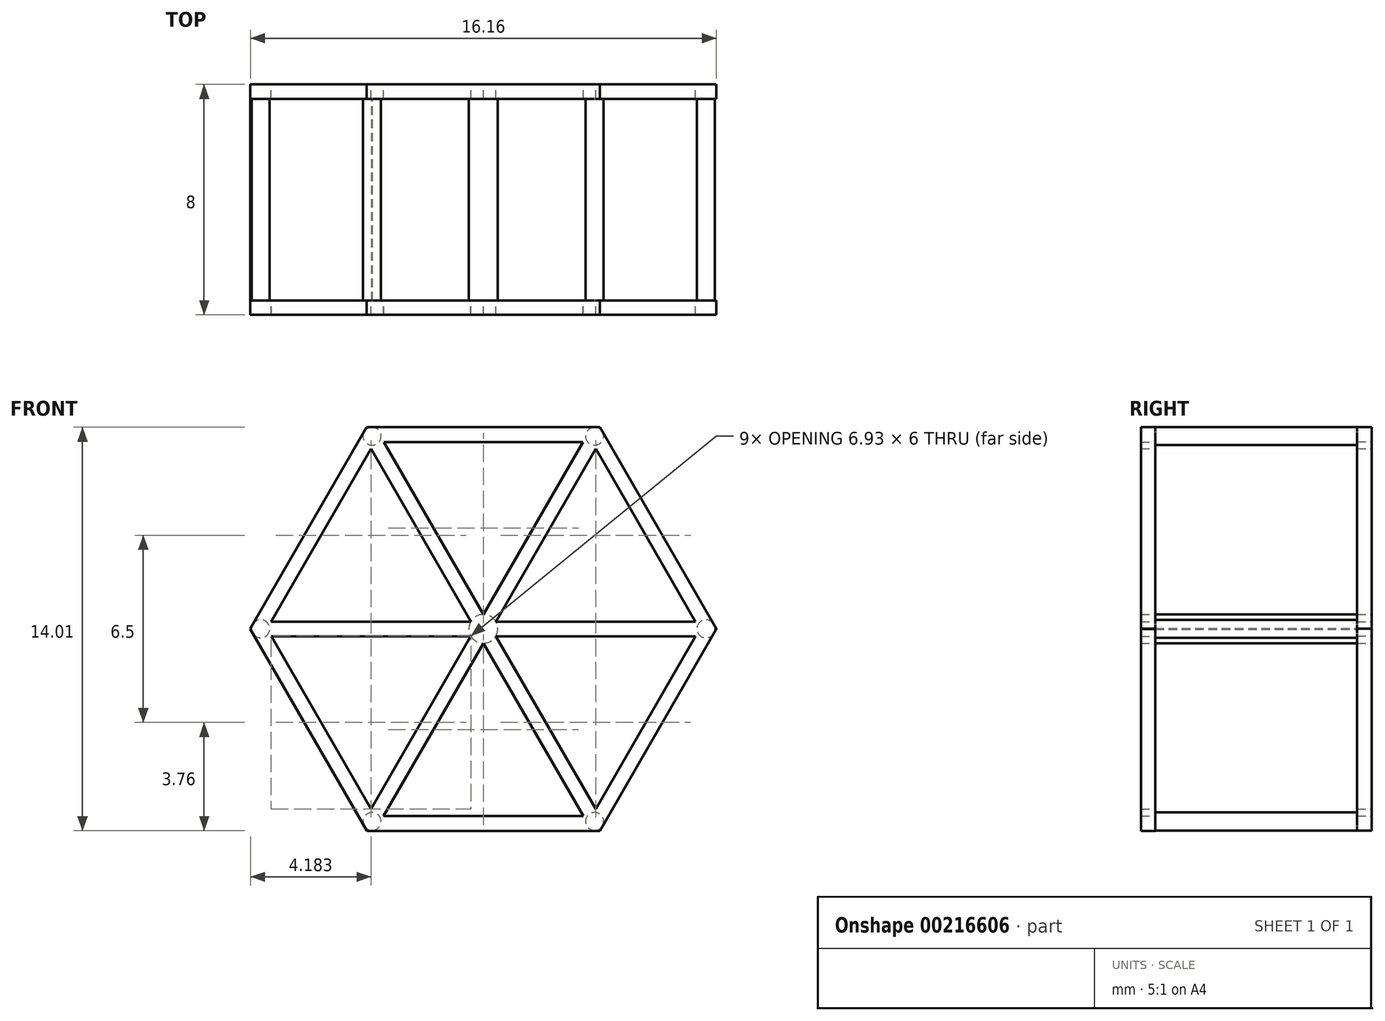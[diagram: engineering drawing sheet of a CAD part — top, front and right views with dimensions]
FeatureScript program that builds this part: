
annotation { "Feature Type Name" : "Feature", "Feature Type Description" : "" }
export const myFeature = defineFeature(function(context is Context, id is Id, definition is map)
    precondition{}
    {
        {
            var Q0;
            Q0=qCreatedBy(makeId("Front.planeOp"),FACE);
            var sketch = newSketch(context, id + "F0", { "sketchPlane" : qUnion([Q0])});
            skLineSegment(sketch, "E0.0", {"start": v(-4.04, 7) * mm, "end": v(4.04, 7) * mm});
            skLineSegment(sketch, "E0.1", {"start": v(4.04, 7) * mm, "end": v(8.08, 0) * mm});
            skLineSegment(sketch, "E0.2", {"start": v(8.08, 0) * mm, "end": v(4.04, -7) * mm});
            skLineSegment(sketch, "E0.3", {"start": v(4.04, -7) * mm, "end": v(-4.04, -7) * mm});
            skLineSegment(sketch, "E0.4", {"start": v(-4.04, -7) * mm, "end": v(-8.08, 0) * mm});
            skLineSegment(sketch, "E0.5", {"start": v(-8.08, 0) * mm, "end": v(-4.04, 7) * mm});
            skPoint(sketch, "E0.0.midPoint", {"position": v(0, 7) * mm});
            skLineSegment(sketch, "E1.0", {"start": v(-3.46, 6.5) * mm, "end": v(3.75, 6.5) * mm});
            skLineSegment(sketch, "E1.1", {"start": v(3.75, 6.5) * mm, "end": v(7.5, 0) * mm});
            skLineSegment(sketch, "E1.2", {"start": v(7.5, 0) * mm, "end": v(3.75, -6.5) * mm});
            skLineSegment(sketch, "E1.3", {"start": v(3.75, -6.5) * mm, "end": v(-3.46, -6.5) * mm});
            skLineSegment(sketch, "E1.4", {"start": v(-3.75, -6.5) * mm, "end": v(-7.36, -0.25) * mm});
            skLineSegment(sketch, "E1.5", {"start": v(-7.36, 0.25) * mm, "end": v(-3.9, 6.25) * mm});
            skPoint(sketch, "E1.0.midPoint", {"position": v(0, 6.5) * mm});
            skLineSegment(sketch, "E2", {"start": v(-0.43, 0.25) * mm, "end": v(-7.36, 0.25) * mm});
            skLineSegment(sketch, "E3", {"start": v(-0.43, -0.25) * mm, "end": v(-7.36, -0.25) * mm});
            skLineSegment(sketch, "E4.1.1", {"start": v(-0.43, -0.25) * mm, "end": v(-3.9, -6.25) * mm});
            skLineSegment(sketch, "E4.2.1", {"start": v(0, -0.5) * mm, "end": v(3.46, -6.5) * mm});
            skLineSegment(sketch, "E4.2.3", {"start": v(0.43, -0.25) * mm, "end": v(3.9, -6.25) * mm});
            skLineSegment(sketch, "E4.2.5", {"start": v(3.75, -6.5) * mm, "end": v(0, -6.5) * mm});
            skLineSegment(sketch, "E4.3.1", {"start": v(0, -0.25) * mm, "end": v(0.14, -0.25) * mm});
            skLineSegment(sketch, "E4.3.3", {"start": v(0.43, 0.25) * mm, "end": v(7.36, 0.25) * mm});
            skLineSegment(sketch, "E4.4.1", {"start": v(0.43, 0.25) * mm, "end": v(3.9, 6.25) * mm});
            skLineSegment(sketch, "E4.4.3", {"start": v(0, 0.5) * mm, "end": v(3.46, 6.5) * mm});
            skLineSegment(sketch, "E4.4.6", {"start": v(-3.75, 6.5) * mm, "end": v(3.75, 6.5) * mm});
            skLineSegment(sketch, "E4.5.1", {"start": v(0, 0.5) * mm, "end": v(-3.46, 6.5) * mm});
            skLineSegment(sketch, "E4.5.5", {"start": v(-3.75, 6.5) * mm, "end": v(3.75, 6.5) * mm});
            skPoint(sketch, "E4.center", {"position": v(0, 0) * mm});
            skPoint(sketch, "E5.orphan", {"position": v(-7.5, 0) * mm});
            skPoint(sketch, "E6.orphan", {"position": v(-0.22, 0.13) * mm});
            skPoint(sketch, "E7.orphan", {"position": v(0.22, 0.13) * mm});
            skPoint(sketch, "E8.orphan", {"position": v(0.22, -0.13) * mm});
            skLineSegment(sketch, "E9.trimOffspring", {"start": v(-0.43, 0.25) * mm, "end": v(-3.9, 6.25) * mm});
            skLineSegment(sketch, "E10.trimOffspring", {"start": v(0, -0.5) * mm, "end": v(-3.46, -6.5) * mm});
            skLineSegment(sketch, "E11.trimOffspring", {"start": v(0.43, -0.25) * mm, "end": v(7.36, -0.25) * mm});
            skPoint(sketch, "E12.orphan", {"position": v(0, -0.25) * mm});
            skLineSegment(sketch, "E13", {"start": v(0, 6.5) * mm, "end": v(0, 0.5) * mm});
            skPoint(sketch, "E14.orphan", {"position": v(-3.75, 6.5) * mm});
            skPoint(sketch, "E15.trimOffspring.end.orphan", {"position": v(0, -7) * mm});
            skSolve(sketch);
        }
        {
            var Q0;
            {var subQ17=sQuery(id+"F0.wireOp",EDGE,"E0.1");Q0=makeQuery(id+"F0.imprint","IMPRINT",FACE,{"disambiguationData":[TD([[makeQuery(id+"F0.imprint","IMPRINT",EDGE,{"derivedFrom":subQ17}),-1.0]])]});}
            extrude(context, id + "F1", {"entities" : qUnion([Q0]), "depth" : .5 * mm});
        }
        {
            var Q0;
            Q0=makeQuery(id+"F1.opExtrude","CAP_FACE",FACE,{"disambiguationData":[OSD([sQuery(id+"F0.wireOp",EDGE,"E0.0"),sQuery(id+"F0.wireOp",EDGE,"E0.1"),sQuery(id+"F0.wireOp",EDGE,"E0.2"),sQuery(id+"F0.wireOp",EDGE,"E0.3"),sQuery(id+"F0.wireOp",EDGE,"E0.4"),sQuery(id+"F0.wireOp",EDGE,"E0.5"),sQuery(id+"F0.wireOp",EDGE,"E2"),sQuery(id+"F0.wireOp",EDGE,"E3"),sQuery(id+"F0.wireOp",EDGE,"E4.1.1"),sQuery(id+"F0.wireOp",EDGE,"E1.4"),sQuery(id+"F0.wireOp",EDGE,"E4.2.1"),sQuery(id+"F0.wireOp",EDGE,"E4.2.3"),sQuery(id+"F0.wireOp",EDGE,"E4.2.5"),sQuery(id+"F0.wireOp",EDGE,"E4.3.3"),sQuery(id+"F0.wireOp",EDGE,"E1.2"),sQuery(id+"F0.wireOp",EDGE,"E4.4.1"),sQuery(id+"F0.wireOp",EDGE,"E4.4.3"),sQuery(id+"F0.wireOp",EDGE,"E1.1"),sQuery(id+"F0.wireOp",EDGE,"E4.5.1"),sQuery(id+"F0.wireOp",EDGE,"E4.5.5"),sQuery(id+"F0.wireOp",EDGE,"E1.5"),sQuery(id+"F0.wireOp",EDGE,"E9.trimOffspring"),sQuery(id+"F0.wireOp",EDGE,"E10.trimOffspring"),sQuery(id+"F0.wireOp",EDGE,"E11.trimOffspring")])],"isStart":false});
            var sketch = newSketch(context, id + "F2", { "sketchPlane" : qUnion([Q0])});
            skCircle(sketch, "E16", {"center": v(0, 0) * mm, "radius": 0.5 * mm});
            skLineSegment(sketch, "E17", {"start": v(-8.08, 0) * mm, "end": v(-7.36, 0.25) * mm});
            skLineSegment(sketch, "E18", {"start": v(-7.36, 0.25) * mm, "end": v(-7.36, -0.25) * mm});
            skLineSegment(sketch, "E19", {"start": v(-7.36, -0.25) * mm, "end": v(-8.08, 0) * mm});
            skLineSegment(sketch, "E20", {"start": v(-8.08, 0) * mm, "end": v(-7.36, 0) * mm});
            skCircle(sketch, "E21", {"center": v(-7.72, 0) * mm, "radius": 0.31 * mm});
            skCircle(sketch, "E22.1.0", {"center": v(-3.86, -6.69) * mm, "radius": 0.31 * mm});
            skCircle(sketch, "E22.2.0", {"center": v(3.86, -6.69) * mm, "radius": 0.31 * mm});
            skCircle(sketch, "E22.3.0", {"center": v(7.72, 0) * mm, "radius": 0.31 * mm});
            skCircle(sketch, "E22.4.0", {"center": v(3.86, 6.69) * mm, "radius": 0.31 * mm});
            skCircle(sketch, "E22.5.0", {"center": v(-3.86, 6.69) * mm, "radius": 0.31 * mm});
            skSolve(sketch);
        }
        {
            var Q0;
            {var subQ0=sQuery(id+"F2.wireOp",EDGE,"E16");var subQ5=makeQuery(id+"F2.imprint","INTERSECT",VERTEX,{"derivedFrom":[makeQuery(id+"F1.opExtrude","CAP_EDGE",EDGE,{"disambiguationData":[OSD([sQuery(id+"F0.wireOp",EDGE,"E4.3.3")])],"isStart":false}),makeQuery(id+"F1.opExtrude","CAP_EDGE",EDGE,{"disambiguationData":[OSD([sQuery(id+"F0.wireOp",EDGE,"E4.4.1")])],"isStart":false}),subQ0]});Q0=makeQuery(id+"F2.imprint","IMPRINT",FACE,{"disambiguationData":[TD([[makeQuery(id+"F2.imprint","IMPRINT",EDGE,{"disambiguationData":[TD([[subQ5,-1.0]])],"derivedFrom":subQ0}),1.0]])]});}
            var Q1;
            {var subQ1=sQuery(id+"F2.wireOp",EDGE,"E17");var subQ3=sQuery(id+"F2.wireOp",EDGE,"E21");var subQ4=makeQuery(id+"F2.imprint","INTERSECT",VERTEX,{"disambiguationData":[OD(0.0)],"derivedFrom":[subQ1,subQ3]});Q1=makeQuery(id+"F2.imprint","IMPRINT",FACE,{"disambiguationData":[TD([[makeQuery(id+"F2.imprint","IMPRINT",EDGE,{"disambiguationData":[TD([[subQ4,-1.0]])],"derivedFrom":subQ3}),-1.0]])]});}
            var Q2;
            {var subQ1=sQuery(id+"F2.wireOp",EDGE,"E19");var subQ3=sQuery(id+"F2.wireOp",EDGE,"E21");var subQ4=makeQuery(id+"F2.imprint","INTERSECT",VERTEX,{"disambiguationData":[OD(1.0)],"derivedFrom":[subQ1,subQ3]});Q2=makeQuery(id+"F2.imprint","IMPRINT",FACE,{"disambiguationData":[TD([[makeQuery(id+"F2.imprint","IMPRINT",EDGE,{"disambiguationData":[TD([[subQ4,1.0]])],"derivedFrom":subQ3}),-1.0]])]});}
            var Q3;
            {var subQ0=sQuery(id+"F2.wireOp",EDGE,"E21");var subQ1=sQuery(id+"F2.wireOp",EDGE,"E17");var subQ2=makeQuery(id+"F2.imprint","INTERSECT",VERTEX,{"disambiguationData":[OD(0.0)],"derivedFrom":[subQ1,subQ0]});Q3=makeQuery(id+"F2.imprint","IMPRINT",FACE,{"disambiguationData":[TD([[makeQuery(id+"F2.imprint","IMPRINT",EDGE,{"disambiguationData":[TD([[subQ2,-1.0]])],"derivedFrom":subQ1}),-1.0]])]});}
            var Q4;
            {var subQ0=sQuery(id+"F2.wireOp",EDGE,"E21");var subQ1=sQuery(id+"F2.wireOp",EDGE,"E19");var subQ2=makeQuery(id+"F2.imprint","INTERSECT",VERTEX,{"disambiguationData":[OD(0.0)],"derivedFrom":[subQ1,subQ0]});Q4=makeQuery(id+"F2.imprint","IMPRINT",FACE,{"disambiguationData":[TD([[makeQuery(id+"F2.imprint","IMPRINT",EDGE,{"disambiguationData":[TD([[subQ2,-1.0]])],"derivedFrom":subQ1}),-1.0]])]});}
            var Q5;
            {var subQ0=sQuery(id+"F2.wireOp",EDGE,"E21");var subQ1=makeQuery(id+"F1.opExtrude","CAP_EDGE",EDGE,{"disambiguationData":[OSD([sQuery(id+"F0.wireOp",EDGE,"E0.5")])],"isStart":false});var subQ2=makeQuery(id+"F2.imprint","INTERSECT",VERTEX,{"disambiguationData":[OD(0.0)],"derivedFrom":[subQ1,subQ0]});Q5=makeQuery(id+"F2.imprint","IMPRINT",FACE,{"disambiguationData":[TD([[makeQuery(id+"F2.imprint","IMPRINT",EDGE,{"disambiguationData":[TD([[subQ2,-1.0]])],"derivedFrom":subQ0}),1.0]])]});}
            var Q6;
            {var subQ0=sQuery(id+"F2.wireOp",EDGE,"E21");var subQ1=makeQuery(id+"F1.opExtrude","CAP_EDGE",EDGE,{"disambiguationData":[OSD([sQuery(id+"F0.wireOp",EDGE,"E0.4")])],"isStart":false});var subQ2=makeQuery(id+"F2.imprint","INTERSECT",VERTEX,{"disambiguationData":[OD(0.0)],"derivedFrom":[subQ1,subQ0]});Q6=makeQuery(id+"F2.imprint","IMPRINT",FACE,{"disambiguationData":[TD([[makeQuery(id+"F2.imprint","IMPRINT",EDGE,{"disambiguationData":[TD([[subQ2,-1.0]])],"derivedFrom":subQ0}),1.0]])]});}
            var Q7;
            {var subQ0=sQuery(id+"F2.wireOp",EDGE,"E22.1.0");var subQ1=makeQuery(id+"F1.opExtrude","CAP_EDGE",EDGE,{"disambiguationData":[OSD([sQuery(id+"F0.wireOp",EDGE,"E0.4")])],"isStart":false});var subQ2=makeQuery(id+"F2.imprint","INTERSECT",VERTEX,{"disambiguationData":[OD(0.0)],"derivedFrom":[subQ1,subQ0]});Q7=makeQuery(id+"F2.imprint","IMPRINT",FACE,{"disambiguationData":[TD([[makeQuery(id+"F2.imprint","IMPRINT",EDGE,{"disambiguationData":[TD([[subQ2,1.0]])],"derivedFrom":subQ0}),1.0]])]});}
            var Q8;
            {var subQ0=sQuery(id+"F2.wireOp",EDGE,"E22.1.0");var subQ1=makeQuery(id+"F1.opExtrude","CAP_EDGE",EDGE,{"disambiguationData":[OSD([sQuery(id+"F0.wireOp",EDGE,"E0.3")])],"isStart":false});var subQ2=makeQuery(id+"F2.imprint","INTERSECT",VERTEX,{"disambiguationData":[OD(0.0)],"derivedFrom":[subQ1,subQ0]});Q8=makeQuery(id+"F2.imprint","IMPRINT",FACE,{"disambiguationData":[TD([[makeQuery(id+"F2.imprint","IMPRINT",EDGE,{"disambiguationData":[TD([[subQ2,-1.0]])],"derivedFrom":subQ0}),1.0]])]});}
            var Q9;
            {var subQ0=sQuery(id+"F2.wireOp",EDGE,"E22.2.0");var subQ1=makeQuery(id+"F1.opExtrude","CAP_EDGE",EDGE,{"disambiguationData":[OSD([sQuery(id+"F0.wireOp",EDGE,"E0.3")])],"isStart":false});var subQ2=makeQuery(id+"F2.imprint","INTERSECT",VERTEX,{"disambiguationData":[OD(0.0)],"derivedFrom":[subQ1,subQ0]});Q9=makeQuery(id+"F2.imprint","IMPRINT",FACE,{"disambiguationData":[TD([[makeQuery(id+"F2.imprint","IMPRINT",EDGE,{"disambiguationData":[TD([[subQ2,1.0]])],"derivedFrom":subQ0}),1.0]])]});}
            var Q10;
            {var subQ0=sQuery(id+"F2.wireOp",EDGE,"E22.2.0");var subQ1=makeQuery(id+"F1.opExtrude","CAP_EDGE",EDGE,{"disambiguationData":[OSD([sQuery(id+"F0.wireOp",EDGE,"E0.2")])],"isStart":false});var subQ2=makeQuery(id+"F2.imprint","INTERSECT",VERTEX,{"disambiguationData":[OD(0.0)],"derivedFrom":[subQ1,subQ0]});Q10=makeQuery(id+"F2.imprint","IMPRINT",FACE,{"disambiguationData":[TD([[makeQuery(id+"F2.imprint","IMPRINT",EDGE,{"disambiguationData":[TD([[subQ2,-1.0]])],"derivedFrom":subQ0}),1.0]])]});}
            var Q11;
            {var subQ0=sQuery(id+"F2.wireOp",EDGE,"E22.3.0");var subQ1=makeQuery(id+"F1.opExtrude","CAP_EDGE",EDGE,{"disambiguationData":[OSD([sQuery(id+"F0.wireOp",EDGE,"E0.2")])],"isStart":false});var subQ2=makeQuery(id+"F2.imprint","INTERSECT",VERTEX,{"disambiguationData":[OD(0.0)],"derivedFrom":[subQ1,subQ0]});Q11=makeQuery(id+"F2.imprint","IMPRINT",FACE,{"disambiguationData":[TD([[makeQuery(id+"F2.imprint","IMPRINT",EDGE,{"disambiguationData":[TD([[subQ2,1.0]])],"derivedFrom":subQ0}),1.0]])]});}
            var Q12;
            {var subQ0=sQuery(id+"F2.wireOp",EDGE,"E22.3.0");var subQ1=makeQuery(id+"F1.opExtrude","CAP_EDGE",EDGE,{"disambiguationData":[OSD([sQuery(id+"F0.wireOp",EDGE,"E0.1")])],"isStart":false});var subQ2=makeQuery(id+"F2.imprint","INTERSECT",VERTEX,{"disambiguationData":[OD(0.0)],"derivedFrom":[subQ1,subQ0]});Q12=makeQuery(id+"F2.imprint","IMPRINT",FACE,{"disambiguationData":[TD([[makeQuery(id+"F2.imprint","IMPRINT",EDGE,{"disambiguationData":[TD([[subQ2,-1.0]])],"derivedFrom":subQ0}),1.0]])]});}
            var Q13;
            {var subQ0=sQuery(id+"F2.wireOp",EDGE,"E22.4.0");var subQ1=makeQuery(id+"F1.opExtrude","CAP_EDGE",EDGE,{"disambiguationData":[OSD([sQuery(id+"F0.wireOp",EDGE,"E0.1")])],"isStart":false});var subQ2=makeQuery(id+"F2.imprint","INTERSECT",VERTEX,{"disambiguationData":[OD(0.0)],"derivedFrom":[subQ1,subQ0]});Q13=makeQuery(id+"F2.imprint","IMPRINT",FACE,{"disambiguationData":[TD([[makeQuery(id+"F2.imprint","IMPRINT",EDGE,{"disambiguationData":[TD([[subQ2,1.0]])],"derivedFrom":subQ0}),1.0]])]});}
            var Q14;
            {var subQ0=sQuery(id+"F2.wireOp",EDGE,"E22.4.0");var subQ1=makeQuery(id+"F1.opExtrude","CAP_EDGE",EDGE,{"disambiguationData":[OSD([sQuery(id+"F0.wireOp",EDGE,"E0.0")])],"isStart":false});var subQ2=makeQuery(id+"F2.imprint","INTERSECT",VERTEX,{"disambiguationData":[OD(0.0)],"derivedFrom":[subQ1,subQ0]});Q14=makeQuery(id+"F2.imprint","IMPRINT",FACE,{"disambiguationData":[TD([[makeQuery(id+"F2.imprint","IMPRINT",EDGE,{"disambiguationData":[TD([[subQ2,-1.0]])],"derivedFrom":subQ0}),1.0]])]});}
            var Q15;
            {var subQ0=sQuery(id+"F2.wireOp",EDGE,"E22.5.0");var subQ1=makeQuery(id+"F1.opExtrude","CAP_EDGE",EDGE,{"disambiguationData":[OSD([sQuery(id+"F0.wireOp",EDGE,"E0.0")])],"isStart":false});var subQ2=makeQuery(id+"F2.imprint","INTERSECT",VERTEX,{"disambiguationData":[OD(0.0)],"derivedFrom":[subQ1,subQ0]});Q15=makeQuery(id+"F2.imprint","IMPRINT",FACE,{"disambiguationData":[TD([[makeQuery(id+"F2.imprint","IMPRINT",EDGE,{"disambiguationData":[TD([[subQ2,1.0]])],"derivedFrom":subQ0}),1.0]])]});}
            var Q16;
            {var subQ0=sQuery(id+"F2.wireOp",EDGE,"E22.5.0");var subQ1=makeQuery(id+"F1.opExtrude","CAP_EDGE",EDGE,{"disambiguationData":[OSD([sQuery(id+"F0.wireOp",EDGE,"E0.5")])],"isStart":false});var subQ2=makeQuery(id+"F2.imprint","INTERSECT",VERTEX,{"disambiguationData":[OD(0.0)],"derivedFrom":[subQ1,subQ0]});Q16=makeQuery(id+"F2.imprint","IMPRINT",FACE,{"disambiguationData":[TD([[makeQuery(id+"F2.imprint","IMPRINT",EDGE,{"disambiguationData":[TD([[subQ2,-1.0]])],"derivedFrom":subQ0}),1.0]])]});}
            var Q17;
            {var subQ0=sQuery(id+"F2.wireOp",EDGE,"E21");var subQ1=sQuery(id+"F2.wireOp",EDGE,"E17");var subQ2=makeQuery(id+"F2.imprint","INTERSECT",VERTEX,{"disambiguationData":[OD(0.0)],"derivedFrom":[subQ1,subQ0]});Q17=makeQuery(id+"F2.imprint","IMPRINT",FACE,{"disambiguationData":[TD([[makeQuery(id+"F2.imprint","IMPRINT",EDGE,{"disambiguationData":[TD([[subQ2,-1.0]])],"derivedFrom":subQ1}),1.0]])]});}
            var Q18;
            {var subQ0=sQuery(id+"F2.wireOp",EDGE,"E21");var subQ1=sQuery(id+"F2.wireOp",EDGE,"E19");var subQ2=makeQuery(id+"F2.imprint","INTERSECT",VERTEX,{"disambiguationData":[OD(0.0)],"derivedFrom":[subQ1,subQ0]});Q18=makeQuery(id+"F2.imprint","IMPRINT",FACE,{"disambiguationData":[TD([[makeQuery(id+"F2.imprint","IMPRINT",EDGE,{"disambiguationData":[TD([[subQ2,-1.0]])],"derivedFrom":subQ1}),1.0]])]});}
            var Q19;
            {var subQ0=sQuery(id+"F2.wireOp",EDGE,"E22.1.0");var subQ1=makeQuery(id+"F1.opExtrude","CAP_EDGE",EDGE,{"disambiguationData":[OSD([sQuery(id+"F0.wireOp",EDGE,"E0.4")])],"isStart":false});var subQ2=makeQuery(id+"F2.imprint","INTERSECT",VERTEX,{"disambiguationData":[OD(0.0)],"derivedFrom":[subQ1,subQ0]});Q19=makeQuery(id+"F2.imprint","IMPRINT",FACE,{"disambiguationData":[TD([[makeQuery(id+"F2.imprint","IMPRINT",EDGE,{"disambiguationData":[TD([[subQ2,-1.0]])],"derivedFrom":subQ0}),1.0]])]});}
            var Q20;
            {var subQ0=sQuery(id+"F2.wireOp",EDGE,"E22.2.0");var subQ1=makeQuery(id+"F1.opExtrude","CAP_EDGE",EDGE,{"disambiguationData":[OSD([sQuery(id+"F0.wireOp",EDGE,"E0.3")])],"isStart":false});var subQ2=makeQuery(id+"F2.imprint","INTERSECT",VERTEX,{"disambiguationData":[OD(0.0)],"derivedFrom":[subQ1,subQ0]});Q20=makeQuery(id+"F2.imprint","IMPRINT",FACE,{"disambiguationData":[TD([[makeQuery(id+"F2.imprint","IMPRINT",EDGE,{"disambiguationData":[TD([[subQ2,-1.0]])],"derivedFrom":subQ0}),1.0]])]});}
            var Q21;
            {var subQ0=sQuery(id+"F2.wireOp",EDGE,"E22.3.0");var subQ1=makeQuery(id+"F1.opExtrude","CAP_EDGE",EDGE,{"disambiguationData":[OSD([sQuery(id+"F0.wireOp",EDGE,"E0.2")])],"isStart":false});var subQ2=makeQuery(id+"F2.imprint","INTERSECT",VERTEX,{"disambiguationData":[OD(0.0)],"derivedFrom":[subQ1,subQ0]});Q21=makeQuery(id+"F2.imprint","IMPRINT",FACE,{"disambiguationData":[TD([[makeQuery(id+"F2.imprint","IMPRINT",EDGE,{"disambiguationData":[TD([[subQ2,-1.0]])],"derivedFrom":subQ0}),1.0]])]});}
            var Q22;
            {var subQ0=sQuery(id+"F2.wireOp",EDGE,"E22.4.0");var subQ1=makeQuery(id+"F1.opExtrude","CAP_EDGE",EDGE,{"disambiguationData":[OSD([sQuery(id+"F0.wireOp",EDGE,"E0.1")])],"isStart":false});var subQ2=makeQuery(id+"F2.imprint","INTERSECT",VERTEX,{"disambiguationData":[OD(0.0)],"derivedFrom":[subQ1,subQ0]});Q22=makeQuery(id+"F2.imprint","IMPRINT",FACE,{"disambiguationData":[TD([[makeQuery(id+"F2.imprint","IMPRINT",EDGE,{"disambiguationData":[TD([[subQ2,-1.0]])],"derivedFrom":subQ0}),1.0]])]});}
            var Q23;
            {var subQ0=sQuery(id+"F2.wireOp",EDGE,"E22.5.0");var subQ1=makeQuery(id+"F1.opExtrude","CAP_EDGE",EDGE,{"disambiguationData":[OSD([sQuery(id+"F0.wireOp",EDGE,"E0.0")])],"isStart":false});var subQ2=makeQuery(id+"F2.imprint","INTERSECT",VERTEX,{"disambiguationData":[OD(0.0)],"derivedFrom":[subQ1,subQ0]});Q23=makeQuery(id+"F2.imprint","IMPRINT",FACE,{"disambiguationData":[TD([[makeQuery(id+"F2.imprint","IMPRINT",EDGE,{"disambiguationData":[TD([[subQ2,-1.0]])],"derivedFrom":subQ0}),1.0]])]});}
            var Q24;
            {var subQ0=sQuery(id+"F2.wireOp",EDGE,"E21");var subQ1=sQuery(id+"F2.wireOp",EDGE,"E17");var subQ2=makeQuery(id+"F2.imprint","INTERSECT",VERTEX,{"disambiguationData":[OD(0.0)],"derivedFrom":[subQ1,subQ0]});Q24=makeQuery(id+"F2.imprint","IMPRINT",FACE,{"disambiguationData":[TD([[makeQuery(id+"F2.imprint","IMPRINT",EDGE,{"disambiguationData":[TD([[subQ2,-1.0]])],"derivedFrom":subQ1}),-1.0]])]});}
            var Q25;
            {var subQ0=sQuery(id+"F2.wireOp",EDGE,"E21");var subQ1=sQuery(id+"F2.wireOp",EDGE,"E19");var subQ2=makeQuery(id+"F2.imprint","INTERSECT",VERTEX,{"disambiguationData":[OD(0.0)],"derivedFrom":[subQ1,subQ0]});Q25=makeQuery(id+"F2.imprint","IMPRINT",FACE,{"disambiguationData":[TD([[makeQuery(id+"F2.imprint","IMPRINT",EDGE,{"disambiguationData":[TD([[subQ2,-1.0]])],"derivedFrom":subQ1}),-1.0]])]});}
            extrude(context, id + "F3", {"entities" : qUnion([Q0, Q1, Q2, Q3, Q4, Q5, Q6, Q7, Q8, Q9, Q10, Q11, Q12, Q13, Q14, Q15, Q16, Q17, Q18, Q19, Q20, Q21, Q22, Q23, Q24, Q25]), "operationType" : NewBodyOperationType.ADD, "depth" : 7 * mm});
        }
        {
            var Q0;
            Q0=makeQuery(id+"F3.opExtrude","CAP_FACE",FACE,{"disambiguationData":[OSD([sQuery(id+"F2.wireOp",EDGE,"E16")])],"isStart":false});
            var sketch = newSketch(context, id + "F4", { "sketchPlane" : qUnion([Q0])});
            skLineSegment(sketch, "E23.0", {"start": v(-4.04, 7) * mm, "end": v(4.04, 7) * mm});
            skLineSegment(sketch, "E23.1", {"start": v(4.04, 7) * mm, "end": v(8.08, 0) * mm});
            skLineSegment(sketch, "E23.2", {"start": v(8.08, 0) * mm, "end": v(4.04, -7) * mm});
            skLineSegment(sketch, "E23.3", {"start": v(4.04, -7) * mm, "end": v(-4.04, -7) * mm});
            skLineSegment(sketch, "E23.4", {"start": v(-4.04, -7) * mm, "end": v(-8.08, 0) * mm});
            skLineSegment(sketch, "E23.5", {"start": v(-8.08, 0) * mm, "end": v(-4.04, 7) * mm});
            skPoint(sketch, "E23.0.midPoint", {"position": v(0, 7) * mm});
            skLineSegment(sketch, "E24", {"start": v(0, 7) * mm, "end": v(0, 6.5) * mm});
            skLineSegment(sketch, "E25.0", {"start": v(-3.75, 6.5) * mm, "end": v(3.75, 6.5) * mm});
            skLineSegment(sketch, "E25.1", {"start": v(3.75, 6.5) * mm, "end": v(7.5, 0) * mm});
            skLineSegment(sketch, "E25.2", {"start": v(7.5, 0) * mm, "end": v(3.75, -6.5) * mm});
            skLineSegment(sketch, "E25.3", {"start": v(3.75, -6.5) * mm, "end": v(-3.75, -6.5) * mm});
            skLineSegment(sketch, "E25.4", {"start": v(-3.75, -6.5) * mm, "end": v(-7.5, 0) * mm});
            skLineSegment(sketch, "E25.5", {"start": v(-7.5, 0) * mm, "end": v(-3.75, 6.5) * mm});
            skPoint(sketch, "E25.0.midPoint", {"position": v(0, 6.5) * mm});
            skLineSegment(sketch, "E26", {"start": v(0, 0) * mm, "end": v(0, 0.5) * mm});
            skLineSegment(sketch, "E27", {"start": v(0, 0) * mm, "end": v(0.43, 0.25) * mm});
            skLineSegment(sketch, "E28", {"start": v(0, 0.5) * mm, "end": v(3.46, 6.5) * mm});
            skLineSegment(sketch, "E29", {"start": v(0.43, 0.25) * mm, "end": v(3.9, 6.25) * mm});
            skLineSegment(sketch, "E30.trimOffspring", {"start": v(0, 6.5) * mm, "end": v(0, 7) * mm});
            skLineSegment(sketch, "E31.1.0", {"start": v(0, 0.5) * mm, "end": v(-3.46, 6.5) * mm});
            skLineSegment(sketch, "E31.1.1", {"start": v(-0.43, 0.25) * mm, "end": v(-3.9, 6.25) * mm});
            skLineSegment(sketch, "E31.2.0", {"start": v(-0.43, 0.25) * mm, "end": v(-7.36, 0.25) * mm});
            skLineSegment(sketch, "E31.2.1", {"start": v(-0.43, -0.25) * mm, "end": v(-7.36, -0.25) * mm});
            skLineSegment(sketch, "E31.3.0", {"start": v(-0.43, -0.25) * mm, "end": v(-3.9, -6.25) * mm});
            skLineSegment(sketch, "E31.3.1", {"start": v(0, -0.5) * mm, "end": v(-3.46, -6.5) * mm});
            skLineSegment(sketch, "E31.4.0", {"start": v(0, -0.5) * mm, "end": v(3.46, -6.5) * mm});
            skLineSegment(sketch, "E31.4.1", {"start": v(0.43, -0.25) * mm, "end": v(3.9, -6.25) * mm});
            skLineSegment(sketch, "E31.5.0", {"start": v(0.43, -0.25) * mm, "end": v(7.36, -0.25) * mm});
            skLineSegment(sketch, "E31.5.1", {"start": v(0.43, 0.25) * mm, "end": v(7.36, 0.25) * mm});
            skPoint(sketch, "E31.center", {"position": v(0, 0) * mm});
            skSolve(sketch);
        }
        {
            var Q0;
            {var subQ1=sQuery(id+"F4.wireOp",EDGE,"E31.1.0");Q0=makeQuery(id+"F4.imprint","IMPRINT",FACE,{"disambiguationData":[TD([[makeQuery(id+"F4.imprint","IMPRINT",EDGE,{"derivedFrom":subQ1}),1.0]])]});}
            var Q1;
            {var subQ1=sQuery(id+"F4.wireOp",EDGE,"E28");Q1=makeQuery(id+"F4.imprint","IMPRINT",FACE,{"disambiguationData":[TD([[makeQuery(id+"F4.imprint","IMPRINT",EDGE,{"derivedFrom":subQ1}),-1.0]])]});}
            var Q2;
            {var subQ3=sQuery(id+"F4.wireOp",EDGE,"E26");Q2=makeQuery(id+"F4.imprint","IMPRINT",FACE,{"disambiguationData":[TD([[makeQuery(id+"F4.imprint","IMPRINT",EDGE,{"derivedFrom":subQ3}),1.0]])]});}
            var Q3;
            {var subQ0=sQuery(id+"F4.wireOp",EDGE,"E26");Q3=makeQuery(id+"F4.imprint","IMPRINT",FACE,{"disambiguationData":[TD([[makeQuery(id+"F4.imprint","IMPRINT",EDGE,{"derivedFrom":subQ0}),-1.0]])]});}
            var Q4;
            {var subQ2=sQuery(id+"F4.wireOp",EDGE,"E31.5.0");Q4=makeQuery(id+"F4.imprint","IMPRINT",FACE,{"disambiguationData":[TD([[makeQuery(id+"F4.imprint","IMPRINT",EDGE,{"derivedFrom":subQ2}),1.0]])]});}
            var Q5;
            {var subQ0=sQuery(id+"F4.wireOp",EDGE,"E31.2.0");Q5=makeQuery(id+"F4.imprint","IMPRINT",FACE,{"disambiguationData":[TD([[makeQuery(id+"F4.imprint","IMPRINT",EDGE,{"derivedFrom":subQ0}),1.0]])]});}
            var Q6;
            {var subQ1=sQuery(id+"F4.wireOp",EDGE,"E31.3.0");Q6=makeQuery(id+"F4.imprint","IMPRINT",FACE,{"disambiguationData":[TD([[makeQuery(id+"F4.imprint","IMPRINT",EDGE,{"derivedFrom":subQ1}),1.0]])]});}
            var Q7;
            {var subQ0=sQuery(id+"F4.wireOp",EDGE,"E31.4.0");Q7=makeQuery(id+"F4.imprint","IMPRINT",FACE,{"disambiguationData":[TD([[makeQuery(id+"F4.imprint","IMPRINT",EDGE,{"derivedFrom":subQ0}),1.0]])]});}
            var Q8;
            {var subQ24=sQuery(id+"F4.wireOp",EDGE,"E23.1");Q8=makeQuery(id+"F4.imprint","IMPRINT",FACE,{"disambiguationData":[TD([[makeQuery(id+"F4.imprint","IMPRINT",EDGE,{"derivedFrom":subQ24}),-1.0]])]});}
            extrude(context, id + "F5", {"entities" : qUnion([Q0, Q1, Q2, Q3, Q4, Q5, Q6, Q7, Q8]), "operationType" : NewBodyOperationType.ADD, "depth" : .5 * mm});
        }
        {
            var Q0;
            Q0=qCreatedBy(makeId("Front.planeOp"),FACE);
            cPlane(context, id + "F6", {"entities" : qUnion([Q0]), "cplaneType" : CPlaneType.OFFSET, "offset" : 7.5 * mm, "width" : 150 * mm, "height" : 150 * mm});
        }
        {
            var Q0;
            Q0=qCreatedBy(id+"F6.planeOp",FACE);
            var sketch = newSketch(context, id + "F7", { "sketchPlane" : qUnion([Q0])});
            skLineSegment(sketch, "E32.0", {"start": v(-4.04, 6.99) * mm, "end": v(4.04, 6.99) * mm});
            skLineSegment(sketch, "E32.1", {"start": v(4.04, 6.99) * mm, "end": v(8.08, -0.01) * mm});
            skLineSegment(sketch, "E32.2", {"start": v(8.08, -0.01) * mm, "end": v(4.04, -7.01) * mm});
            skLineSegment(sketch, "E32.3", {"start": v(4.04, -7.01) * mm, "end": v(-4.04, -7.01) * mm});
            skLineSegment(sketch, "E32.4", {"start": v(-4.04, -7.01) * mm, "end": v(-8.08, -0.01) * mm});
            skLineSegment(sketch, "E32.5", {"start": v(-8.08, -0.01) * mm, "end": v(-4.04, 6.99) * mm});
            skPoint(sketch, "E32.0.midPoint", {"position": v(0, 6.99) * mm});
            skLineSegment(sketch, "E33", {"start": v(0, 6.99) * mm, "end": v(0, 6.49) * mm});
            skLineSegment(sketch, "E34.0", {"start": v(-3.75, 6.49) * mm, "end": v(3.75, 6.49) * mm});
            skLineSegment(sketch, "E34.1", {"start": v(3.75, 6.49) * mm, "end": v(7.5, -0.01) * mm});
            skLineSegment(sketch, "E34.2", {"start": v(7.5, -0.01) * mm, "end": v(3.75, -6.51) * mm});
            skLineSegment(sketch, "E34.3", {"start": v(3.75, -6.51) * mm, "end": v(-3.75, -6.51) * mm});
            skLineSegment(sketch, "E34.4", {"start": v(-3.75, -6.51) * mm, "end": v(-7.5, -0.01) * mm});
            skLineSegment(sketch, "E34.5", {"start": v(-7.5, -0.01) * mm, "end": v(-3.75, 6.49) * mm});
            skPoint(sketch, "E34.0.midPoint", {"position": v(0, 6.49) * mm});
            skLineSegment(sketch, "E35", {"start": v(0, -0.01) * mm, "end": v(0, 0.49) * mm});
            skLineSegment(sketch, "E36", {"start": v(0, -0.01) * mm, "end": v(0.43, 0.24) * mm});
            skLineSegment(sketch, "E37", {"start": v(0, 0.49) * mm, "end": v(3.46, 6.49) * mm});
            skLineSegment(sketch, "E38", {"start": v(0.43, 0.24) * mm, "end": v(3.9, 6.24) * mm});
            skLineSegment(sketch, "E39.trimOffspring", {"start": v(0, 6.49) * mm, "end": v(0, 6.99) * mm});
            skLineSegment(sketch, "E40.1.0", {"start": v(0, 0.49) * mm, "end": v(-3.46, 6.49) * mm});
            skLineSegment(sketch, "E40.1.1", {"start": v(-0.43, 0.24) * mm, "end": v(-3.9, 6.24) * mm});
            skLineSegment(sketch, "E40.2.0", {"start": v(-0.43, 0.24) * mm, "end": v(-7.36, 0.24) * mm});
            skLineSegment(sketch, "E40.2.1", {"start": v(-0.43, -0.26) * mm, "end": v(-7.36, -0.26) * mm});
            skLineSegment(sketch, "E40.3.0", {"start": v(-0.43, -0.26) * mm, "end": v(-3.9, -6.26) * mm});
            skLineSegment(sketch, "E40.3.1", {"start": v(0, -0.51) * mm, "end": v(-3.46, -6.51) * mm});
            skLineSegment(sketch, "E40.4.0", {"start": v(0, -0.51) * mm, "end": v(3.46, -6.51) * mm});
            skLineSegment(sketch, "E40.4.1", {"start": v(0.43, -0.26) * mm, "end": v(3.9, -6.26) * mm});
            skLineSegment(sketch, "E40.5.0", {"start": v(0.43, -0.26) * mm, "end": v(7.36, -0.26) * mm});
            skLineSegment(sketch, "E40.5.1", {"start": v(0.43, 0.24) * mm, "end": v(7.36, 0.24) * mm});
            skPoint(sketch, "E40.center", {"position": v(0, -0.01) * mm});
            skSolve(sketch);
        }
        {
            var Q0;
            Q0 = qSketchRegion(id + "F7", true);
            var Q1;
            Q1=makeQuery(id+"F7.imprint","IMPRINT",FACE,{"disambiguationData":[TD([[makeQuery(id+"F7.imprint","IMPRINT",EDGE,{"derivedFrom":sQuery(id+"F7.wireOp",EDGE,"E35")}),1.0]])]});
            var Q2;
            Q2=makeQuery(id+"F7.imprint","IMPRINT",FACE,{"disambiguationData":[TD([[makeQuery(id+"F7.imprint","IMPRINT",EDGE,{"derivedFrom":sQuery(id+"F7.wireOp",EDGE,"E35")}),-1.0]])]});
            extrude(context, id + "F8", {"entities" : qUnion([Q0, Q1, Q2]), "operationType" : NewBodyOperationType.ADD, "depth" : .5 * mm});
        }
    });
